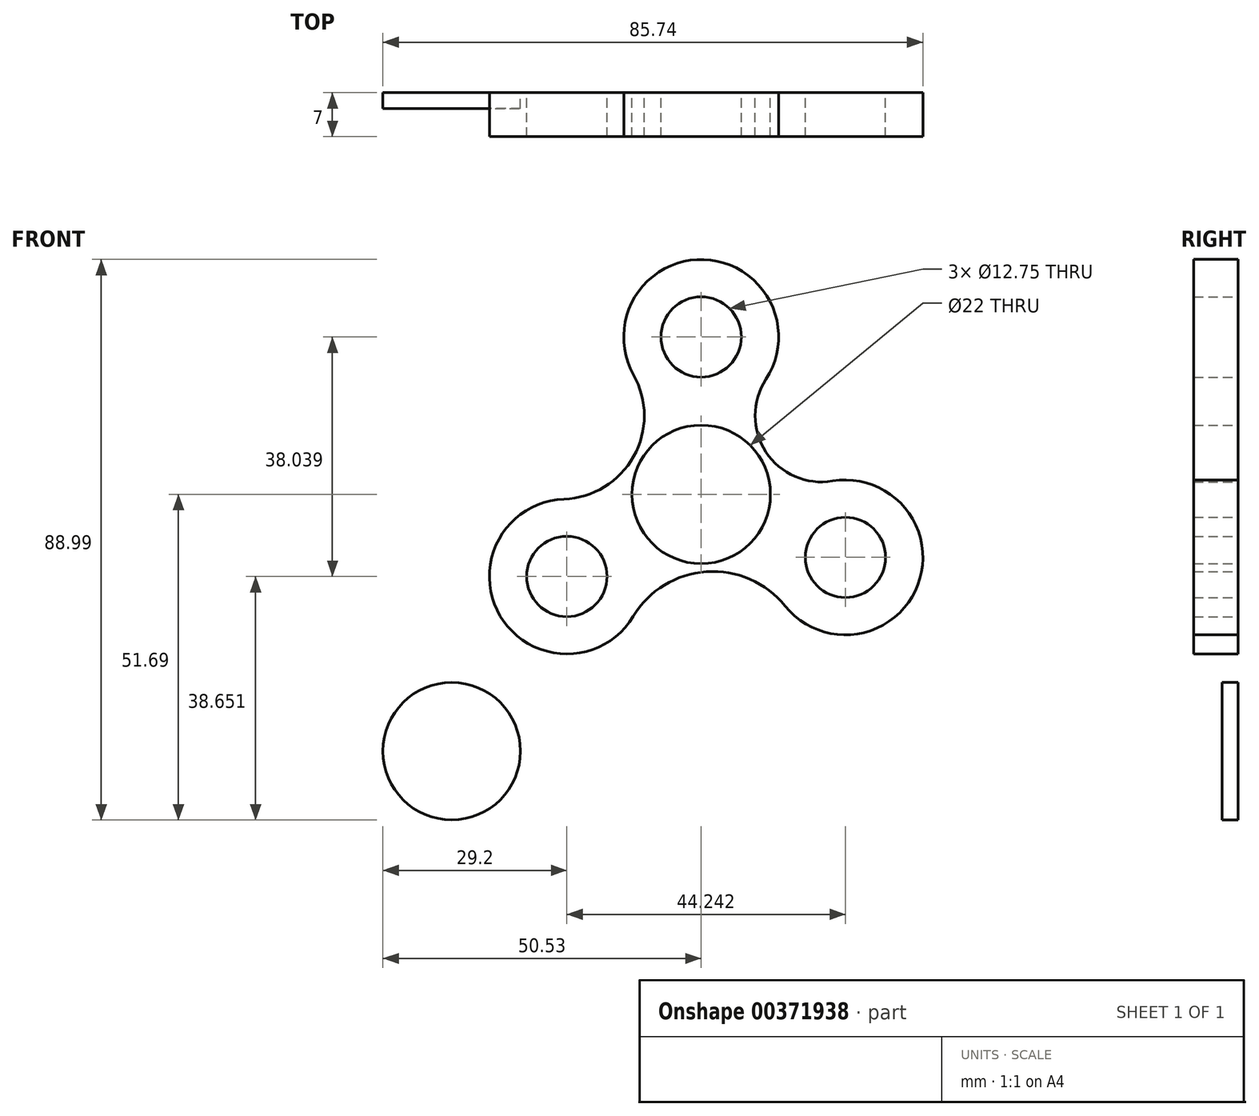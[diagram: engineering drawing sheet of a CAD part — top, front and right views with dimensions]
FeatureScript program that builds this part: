
annotation { "Feature Type Name" : "Feature", "Feature Type Description" : "" }
export const myFeature = defineFeature(function(context is Context, id is Id, definition is map)
    precondition{}
    {
        {
            var Q0;
            Q0=qCreatedBy(makeId("Front.planeOp"),FACE);
            var sketch = newSketch(context, id + "F0", { "sketchPlane" : qUnion([Q0])});
            skCircle(sketch, "E0", {"center": v(0, 0) * mm, "radius": 4 * mm});
            skCircle(sketch, "E1", {"center": v(0, 0) * mm, "radius": 11 * mm});
            skCircle(sketch, "E2", {"center": v(0, 25) * mm, "radius": 12.3 * mm});
            skCircle(sketch, "E3", {"center": v(-21.33, -13.04) * mm, "radius": 12.3 * mm});
            skCircle(sketch, "E4", {"center": v(22.91, -10) * mm, "radius": 12.3 * mm});
            skCircle(sketch, "E5", {"center": v(0, 0) * mm, "radius": 12.3 * mm});
            skArc(sketch, "E6", {"start": v(10.3, 18.26) * mm, "mid": v(10.3, 6.74) * mm, "end": v(20.86, 2.12) * mm});
            skArc(sketch, "E7", {"start": v(13.34, -17.73) * mm, "mid": v(0.84, -12.27) * mm, "end": v(-10.8, -19.38) * mm});
            skArc(sketch, "E8", {"start": v(-21.8, -0.75) * mm, "mid": v(-10.73, 6.02) * mm, "end": v(-10.73, 18.98) * mm});
            skCircle(sketch, "E9", {"center": v(0, 25) * mm, "radius": 6.38 * mm});
            skCircle(sketch, "E10", {"center": v(22.91, -10) * mm, "radius": 6.38 * mm});
            skCircle(sketch, "E11", {"center": v(-21.33, -13.04) * mm, "radius": 6.38 * mm});
            skSolve(sketch);
        }
        {
            var Q0;
            Q0 = qSketchRegion(id + "F0", true);
            var Q1;
            Q1=makeQuery(id+"F0.imprint","IMPRINT",FACE,{"disambiguationData":[TD([[makeQuery(id+"F0.imprint","IMPRINT",EDGE,{"derivedFrom":sQuery(id+"F0.wireOp",EDGE,"58e0fc1b-89c6-4e03-be43-a5795ae32cd7.1.0")}),-1.0]])]});
            var Q2;
            Q2=makeQuery(id+"F0.imprint","IMPRINT",FACE,{"disambiguationData":[TD([[makeQuery(id+"F0.imprint","IMPRINT",EDGE,{"derivedFrom":sQuery(id+"F0.wireOp",EDGE,"w5UxgXI9-8RxX-3LTh-38it-XEFhzCoGaVPx")}),-1.0]])]});
            var Q3;
            Q3=makeQuery(id+"F0.imprint","IMPRINT",FACE,{"disambiguationData":[TD([[makeQuery(id+"F0.imprint","IMPRINT",EDGE,{"derivedFrom":sQuery(id+"F0.wireOp",EDGE,"58e0fc1b-89c6-4e03-be43-a5795ae32cd7.2.0")}),-1.0]])]});
            extrude(context, id + "F1", {"entities" : qUnion([Q0, Q1, Q2, Q3]), "depth" : 7 * mm});
        }
        {
            var Q0;
            Q0=qCreatedBy(makeId("Front.planeOp"),FACE);
            var sketch = newSketch(context, id + "F2", { "sketchPlane" : qUnion([Q0])});
            skCircle(sketch, "E12", {"center": v(-39.62, -40.77) * mm, "radius": 10.91 * mm});
            skCircle(sketch, "E13", {"center": v(-39.62, -40.77) * mm, "radius": 4.5 * mm});
            skSolve(sketch);
        }
        {
            var Q0;
            Q0=makeQuery(id+"F2.imprint","IMPRINT",FACE,{"disambiguationData":[TD([[makeQuery(id+"F2.imprint","IMPRINT",EDGE,{"derivedFrom":sQuery(id+"F2.wireOp",EDGE,"E12")}),1.0]])]});
            var Q1;
            Q1=makeQuery(id+"F2.imprint","IMPRINT",FACE,{"disambiguationData":[TD([[makeQuery(id+"F2.imprint","IMPRINT",EDGE,{"derivedFrom":sQuery(id+"F2.wireOp",EDGE,"E13")}),1.0]])]});
            extrude(context, id + "F3", {"entities" : qUnion([Q0, Q1]), "depth" : 2.5 * mm, "offsetDistance" : 25 * mm});
        }
        {
            var Q0;
            Q0=sQuery(id+"F2.wireOp",EDGE,"E13");
            extrude(context, id + "F4", {"bodyType" : ToolBodyType.SURFACE, "operationType" : NewBodyOperationType.ADD, "surfaceEntities" : qUnion([Q0]), "depth" : 3 * mm, "offsetDistance" : 25 * mm});
        }
    });
